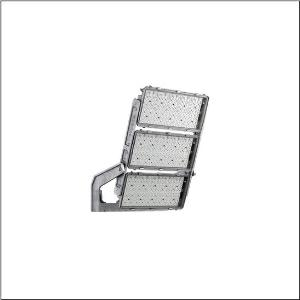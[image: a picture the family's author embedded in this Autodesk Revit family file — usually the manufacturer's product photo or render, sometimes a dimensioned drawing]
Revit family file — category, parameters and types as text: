
# Revit family: floodlight_fl_11_maxi_pro_remote___pl43_5xa779427a01aa_51b3
name_source: partatom
category: Lighting Fixtures
units: mm (PartAtom-declared; Revit-internal decimal feet)

## family parameters
Cut with Voids When Loaded = No
Host = Face
Light Source = No
Part Type = Normal
Room Calculation Point = No
Round Connector Dimension = Use Diameter
Shared = No

## types (1)
- --- (1 x LED, 177380 lm, 1425.5 W, 5000K)
    Apparent Load = 1425 VA
    CIE Flux Codes = 25 74 99 100 100
    Color Rendering = 70
    Color Temperature = 5000K
    Default Elevation = 1800 mm
    Description = Floodlight FL 11  maxi  pro Remote floodlight; light control with lens of PMMA; cover panel of toughened safety glass, transparent; light distribution: PL43, asymmetric direct distribution, LEDcolour temperature: 5000K, rated luminous flux: 177.380lm, colour rendering: CRI > 70, light colour: 750; luminous efficacy: 124lm/W; brightness control: DALI 2 (1 DALI address); with terminal, 8-pole, max. 2.5mm², mains connection: 220..240V/380..400V AC, 50/60Hz, surge voltage resistance: line to ground: 10kV, ECG replaceable separately, LED unit replaceable without ESD environment, dustproof LED module, dimming range 10..100%, no afterglow with DALI off / DMX off command; 1426W floodlight with 2x LED unit of diecast aluminium, coated grey; length: 713mm / width: 651mm / height: 338mm; mounting bracket, of diecast aluminium, uncoated, natural, equipment: Power, protection rating (complete): IP66; insulation class (complete): insulation class I (protective earthing); certification: CE, ENEC, VDE; ball protection: ball impact resistance with accessories, impact resistance: IK07; rated ambient temperature 10°C, only for outdoor installations, permissible operating ambient temperature: -40..+30°C, permissible storage temperature: -40..+85°C; packaging unit: 1 piece

Light Distribution: PL43
    Height = 320 mm
    Lamp = 1 x LED
    Lamp Light Flux = 177380 lm
    Lamp Power = 1425.5 W
    Lamp count = 1
    Length = 1002 mm
    Luminous efficacy = 124 lm/W
    Manufacturer = Siteco
    ModVariant = No
    Model = 5XA779427A01AA
    Mounting Place = Ceiling
    Mounting Type = Surface mounted
    Number of Poles = 1
    OnlyDefault = Yes
    Power Factor = 1
    Product Name = Floodlight FL 11 maxi pro Remote | PL43
    Product group = floodlight | ceiling mounted
    ProductGroupID = 302
    Protection Class = Protection class I
    Protection Degree = IP 66
    RLX_Detail_Level = 1
    RLX_Emergency_Light_Flux = 0 lm
    RLX_Emergency_Type = 0
    RLX_Emergency_Type_DB = No
    RlxData = <blob elided: 52429 chars, md5=9c6276cd>
    Socket = socket
    Standby Power = 0 W
    System Light Flux = 177380 lm
    System Power = 1425 W
    Type Comments = factory setting: luminous flux: 100 % | dim-lin: 254 | 980 mA
    Type Image = l_1006784.jpg
    URL = http://relux.com
    VarID = @adj_026889
    Voltage = 0 V
    Weight = 0.00 kg
    Width = 655 mm

## geometry (parser evidence)
native form markers: Blend x4, Sweep x11
no freeform markers — native parametric forms only
